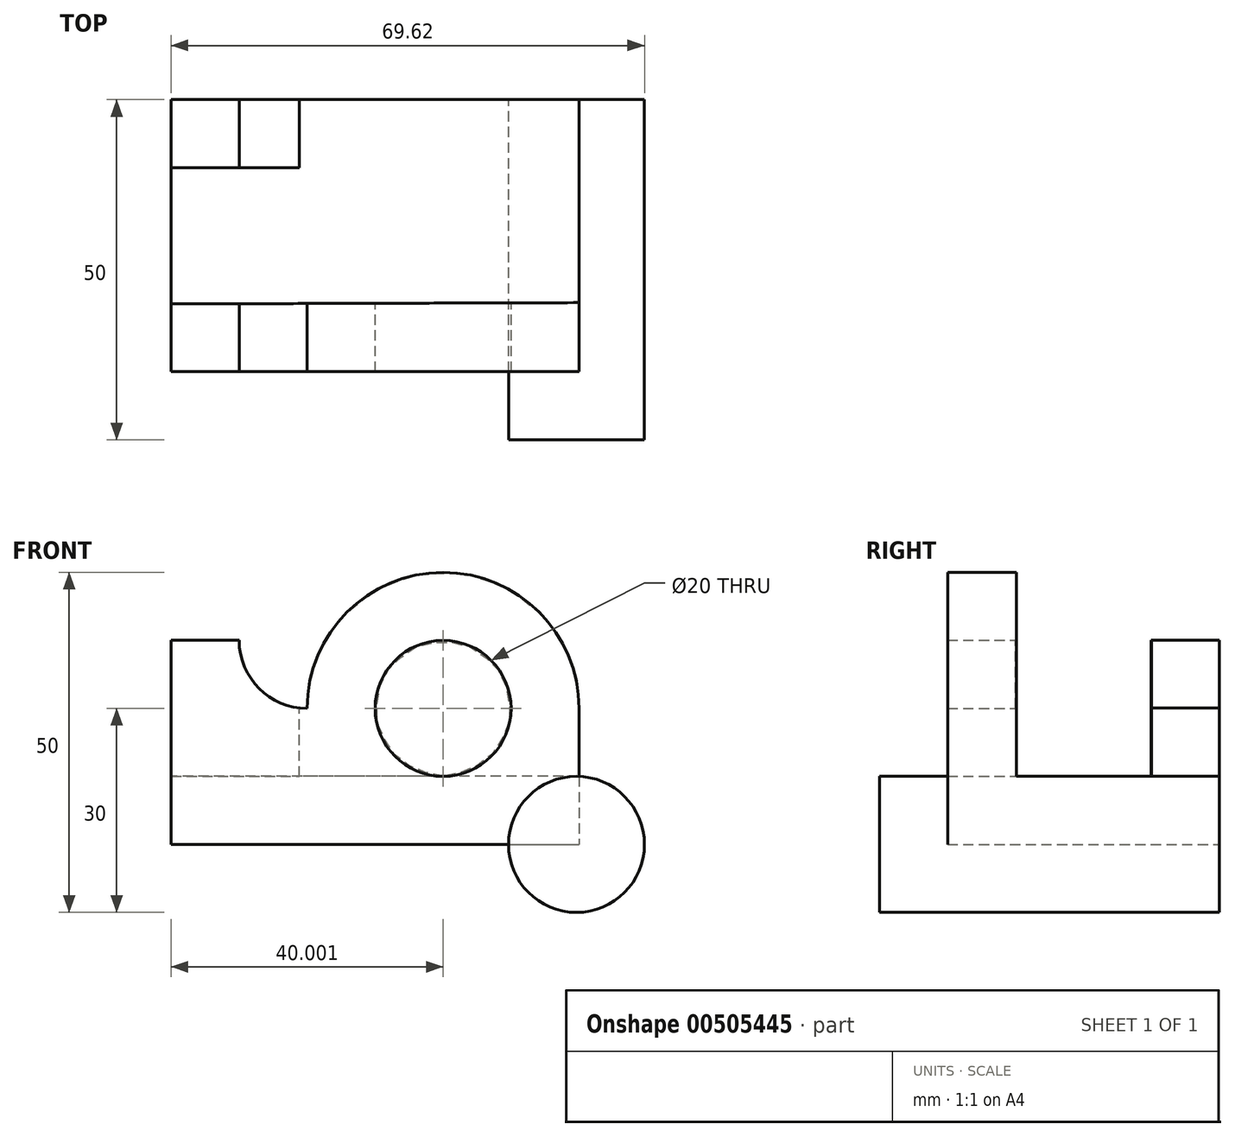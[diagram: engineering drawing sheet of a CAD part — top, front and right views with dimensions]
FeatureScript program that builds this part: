
annotation { "Feature Type Name" : "Feature", "Feature Type Description" : "" }
export const myFeature = defineFeature(function(context is Context, id is Id, definition is map)
    precondition{}
    {
        {
            var Q0;
            Q0=qCreatedBy(makeId("Front.planeOp"),FACE);
            var sketch = newSketch(context, id + "F0", { "sketchPlane" : qUnion([Q0])});
            skLineSegment(sketch, "E0", {"start": v(-26.38, 0) * mm, "end": v(33.62, 0) * mm});
            skLineSegment(sketch, "E1", {"start": v(-26.38, 0) * mm, "end": v(-26.38, 30) * mm});
            skLineSegment(sketch, "E2", {"start": v(-26.38, 30) * mm, "end": v(-16.38, 30) * mm});
            skLineSegment(sketch, "E3", {"start": v(-16.38, 30) * mm, "end": v(-16.38, 30) * mm});
            skLineSegment(sketch, "E4", {"start": v(-6.38, 20) * mm, "end": v(-6.38, 20) * mm});
            skPoint(sketch, "E5.visualSharp", {"position": v(-16.38, 20) * mm});
            skArc(sketch, "E5.filletArc", {"start": v(-16.38, 30) * mm, "mid": v(-13.45, 22.93) * mm, "end": v(-6.38, 20) * mm});
            skLineSegment(sketch, "E6", {"start": v(-6.38, 20) * mm, "end": v(-6.38, 10) * mm});
            skLineSegment(sketch, "E7", {"start": v(-6.38, 10) * mm, "end": v(33.62, 10) * mm});
            skLineSegment(sketch, "E8", {"start": v(33.62, 10) * mm, "end": v(33.62, 0) * mm});
            skLineSegment(sketch, "E9", {"start": v(-6.38, 20) * mm, "end": v(13.62, 20) * mm, "construction": true});
            skPoint(sketch, "E9.endSnap0", {"position": v(13.62, 10) * mm});
            skCircle(sketch, "E10", {"center": v(13.62, 20) * mm, "radius": 10 * mm});
            skArc(sketch, "E11", {"start": v(-6.38, 20) * mm, "mid": v(13.62, 40) * mm, "end": v(33.62, 20) * mm});
            skLineSegment(sketch, "E12", {"start": v(33.62, 20) * mm, "end": v(33.62, 10) * mm});
            skSolve(sketch);
        }
        {
            var Q0;
            Q0 = qSketchRegion(id + "F0", true);
            extrude(context, id + "F1", {"entities" : qUnion([Q0]), "depth" : 40 * mm});
        }
        {
            var Q0;
            Q0=qCreatedBy(makeId("Top.planeOp"),FACE);
            cPlane(context, id + "F2", {"entities" : qUnion([Q0]), "cplaneType" : CPlaneType.OFFSET, "offset" : 40 * mm, "width" : 150 * mm, "height" : 150 * mm});
        }
        {
            var Q0;
            Q0=qCreatedBy(id+"F2.planeOp",FACE);
            var sketch = newSketch(context, id + "F3", { "sketchPlane" : qUnion([Q0])});
            skLineSegment(sketch, "E13", {"start": v(0, -40) * mm, "end": v(0, -30) * mm, "construction": true});
            skLineSegment(sketch, "E14", {"start": v(34.56, -10.03) * mm, "end": v(34.56, -29.84) * mm});
            skLineSegment(sketch, "E15", {"start": v(34.56, 0.16) * mm, "end": v(34.56, -10.03) * mm});
            skLineSegment(sketch, "E16", {"start": v(-16.44, -30) * mm, "end": v(34.56, -29.84) * mm});
            skLineSegment(sketch, "E17", {"start": v(-16.44, -30) * mm, "end": v(-27.44, -30.03) * mm});
            skLineSegment(sketch, "E18", {"start": v(-27.44, -30.03) * mm, "end": v(-27.5, -10.03) * mm});
            skLineSegment(sketch, "E19", {"start": v(-27.5, -10.03) * mm, "end": v(-7.5, -9.97) * mm});
            skLineSegment(sketch, "E20", {"start": v(-7.5, -9.97) * mm, "end": v(-7.53, 0.03) * mm});
            skLineSegment(sketch, "E21", {"start": v(-7.53, 0.03) * mm, "end": v(34.56, 0.16) * mm});
            skSolve(sketch);
        }
        {
            var Q0;
            Q0 = qSketchRegion(id + "F3", true);
            extrude(context, id + "F4", {"entities" : qUnion([Q0]), "operationType" : NewBodyOperationType.REMOVE, "oppositeDirection" : true, "depth" : 30 * mm});
        }
        {
            var Q0;
            Q0=qCreatedBy(makeId("Front.planeOp"),FACE);
            var sketch = newSketch(context, id + "F5", { "sketchPlane" : qUnion([Q0])});
            skCircle(sketch, "E22", {"center": v(33.24, 0) * mm, "radius": 10 * mm});
            skSolve(sketch);
        }
        {
            var Q0;
            Q0 = qSketchRegion(id + "F5", true);
            extrude(context, id + "F6", {"entities" : qUnion([Q0]), "depth" : 50 * mm});
        }
    });
